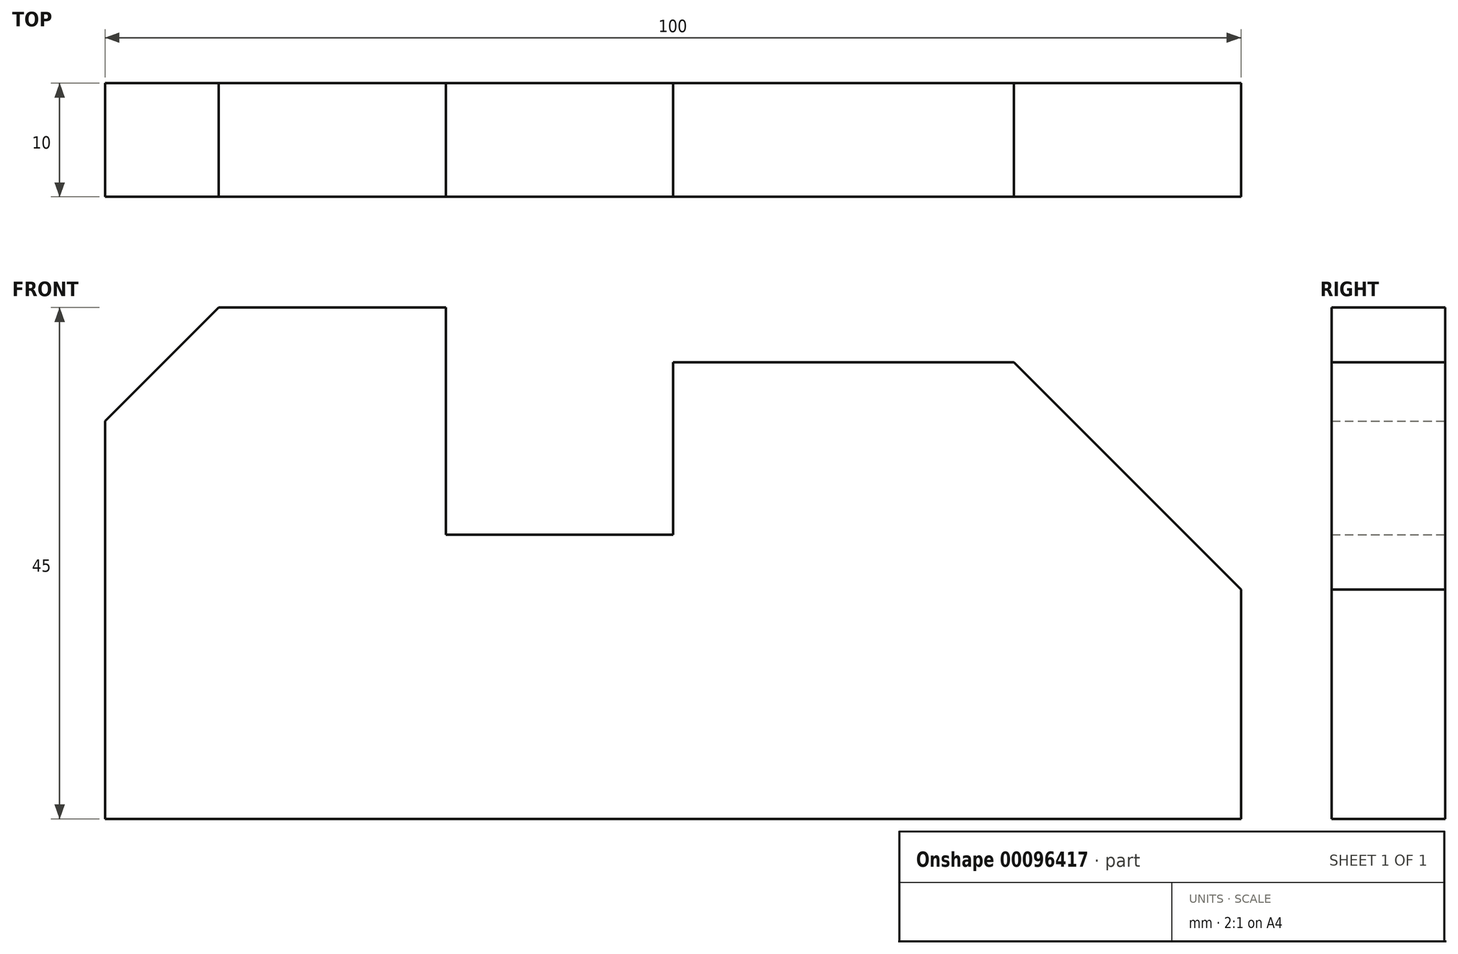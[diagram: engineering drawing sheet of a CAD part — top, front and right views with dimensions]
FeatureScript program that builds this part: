
annotation { "Feature Type Name" : "Feature", "Feature Type Description" : "" }
export const myFeature = defineFeature(function(context is Context, id is Id, definition is map)
    precondition{}
    {
        {
            var Q0;
            Q0=qCreatedBy(makeId("Front.planeOp"),FACE);
            var sketch = newSketch(context, id + "F0", { "sketchPlane" : qUnion([Q0])});
            skLineSegment(sketch, "E0", {"start": v(0, 0) * mm, "end": v(100, 0) * mm});
            skLineSegment(sketch, "E1", {"start": v(100, 0) * mm, "end": v(100, 20.2) * mm});
            skLineSegment(sketch, "E2", {"start": v(100, 20.2) * mm, "end": v(80, 40.2) * mm});
            skLineSegment(sketch, "E3", {"start": v(80, 40.2) * mm, "end": v(50, 40.2) * mm});
            skLineSegment(sketch, "E4", {"start": v(50, 40.2) * mm, "end": v(50, 25) * mm});
            skLineSegment(sketch, "E5", {"start": v(50, 25) * mm, "end": v(30, 25) * mm});
            skLineSegment(sketch, "E6", {"start": v(30, 25) * mm, "end": v(30, 45) * mm});
            skLineSegment(sketch, "E7", {"start": v(30, 45) * mm, "end": v(10, 45) * mm});
            skLineSegment(sketch, "E8", {"start": v(10, 45) * mm, "end": v(0, 35) * mm});
            skLineSegment(sketch, "E9", {"start": v(0, 35) * mm, "end": v(0, 0) * mm});
            skSolve(sketch);
        }
        {
            var Q0;
            Q0 = qSketchRegion(id + "F0", true);
            extrude(context, id + "F1", {"entities" : qUnion([Q0]), "depth" : 10 * mm});
        }
    });
